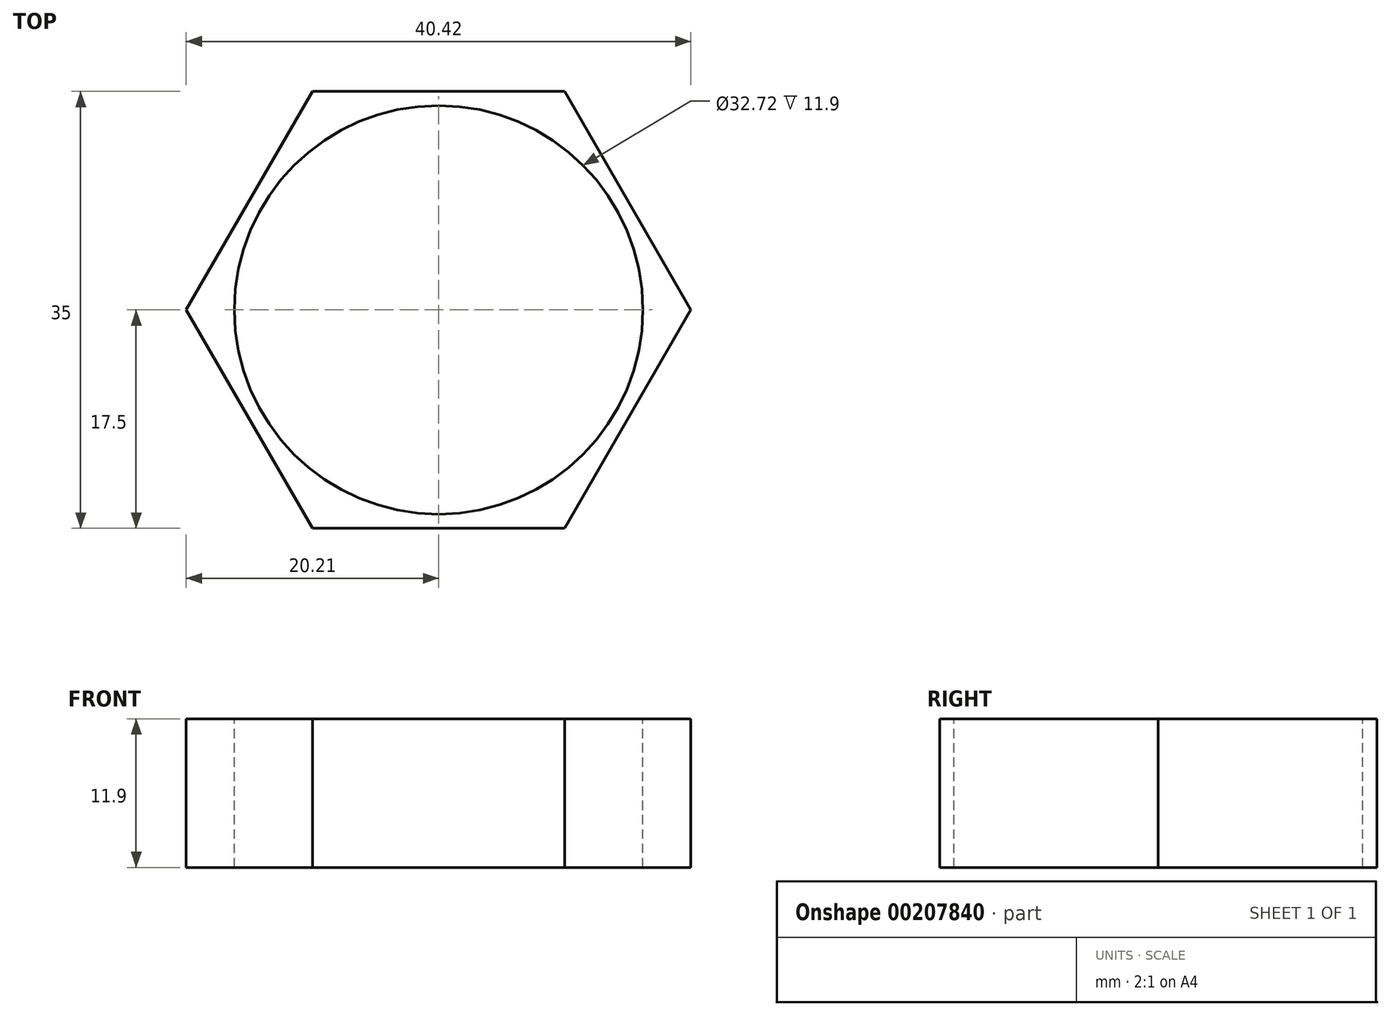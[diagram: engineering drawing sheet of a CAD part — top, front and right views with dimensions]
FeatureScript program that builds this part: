
annotation { "Feature Type Name" : "Feature", "Feature Type Description" : "" }
export const myFeature = defineFeature(function(context is Context, id is Id, definition is map)
    precondition{}
    {
        {
            var Q0;
            Q0=qCreatedBy(makeId("Top.planeOp"),FACE);
            var sketch = newSketch(context, id + "F0", { "sketchPlane" : qUnion([Q0])});
            skCircle(sketch, "E0.cCircle", {"center": v(0, 0) * mm, "radius": 17.5 * mm, "construction": true});
            skLineSegment(sketch, "E0.0", {"start": v(20.2, 0) * mm, "end": v(10.1, -17.5) * mm});
            skLineSegment(sketch, "E0.1", {"start": v(10.1, -17.5) * mm, "end": v(-10.1, -17.5) * mm});
            skLineSegment(sketch, "E0.2", {"start": v(-10.1, -17.5) * mm, "end": v(-20.2, 0) * mm});
            skLineSegment(sketch, "E0.3", {"start": v(-20.2, 0) * mm, "end": v(-10.1, 17.5) * mm});
            skLineSegment(sketch, "E0.4", {"start": v(-10.1, 17.5) * mm, "end": v(10.1, 17.5) * mm});
            skLineSegment(sketch, "E0.5", {"start": v(10.1, 17.5) * mm, "end": v(20.2, 0) * mm});
            skPoint(sketch, "E0.0.midPoint", {"position": v(15.16, -8.75) * mm});
            skSolve(sketch);
        }
        {
            var Q0;
            Q0=makeQuery(id+"F0.imprint","IMPRINT",FACE,{"disambiguationData":[TD([[makeQuery(id+"F0.imprint","IMPRINT",EDGE,{"derivedFrom":sQuery(id+"F0.wireOp",EDGE,"E0.0")}),-1.0]])]});
            extrude(context, id + "F1", {"entities" : qUnion([Q0]), "depth" : 11.9 * mm});
        }
        {
            var Q0;
            Q0=makeQuery(id+"F1.opExtrude","CAP_FACE",FACE,{"disambiguationData":[OSD([sQuery(id+"F0.wireOp",EDGE,"E0.0"),sQuery(id+"F0.wireOp",EDGE,"E0.1"),sQuery(id+"F0.wireOp",EDGE,"E0.2"),sQuery(id+"F0.wireOp",EDGE,"E0.3"),sQuery(id+"F0.wireOp",EDGE,"E0.4"),sQuery(id+"F0.wireOp",EDGE,"E0.5")])],"isStart":false});
            var sketch = newSketch(context, id + "F2", { "sketchPlane" : qUnion([Q0])});
            skCircle(sketch, "E1", {"center": v(0, 0) * mm, "radius": 16.36 * mm});
            skSolve(sketch);
        }
        {
            var Q0;
            Q0 = qSketchRegion(id + "F2", true);
            extrude(context, id + "F3", {"entities" : qUnion([Q0]), "operationType" : NewBodyOperationType.REMOVE, "endBound" : BoundingType.THROUGH_ALL, "oppositeDirection" : true, "depth" : 25 * mm});
        }
    });
